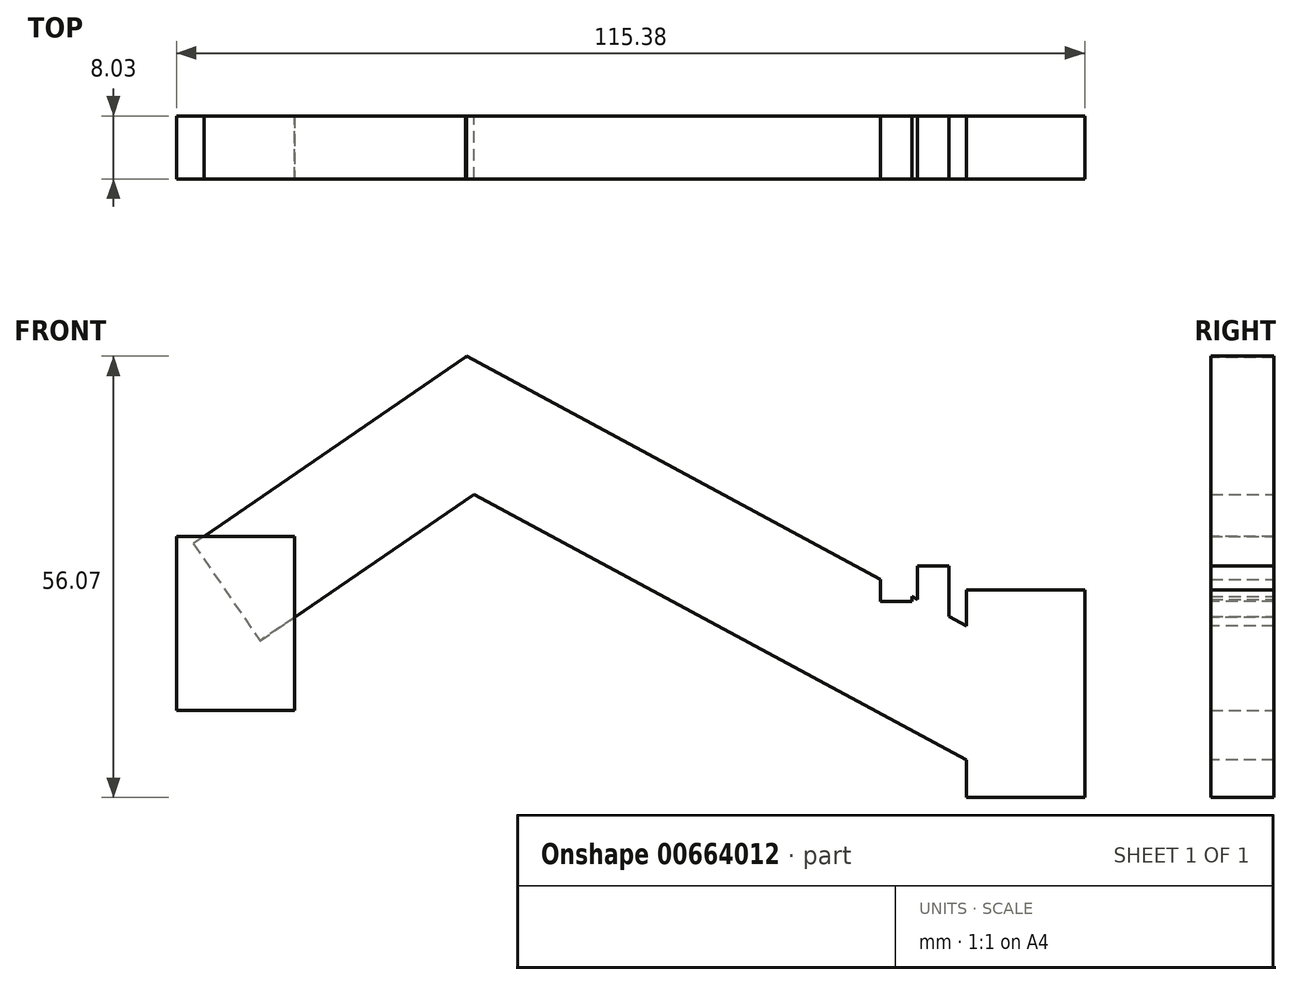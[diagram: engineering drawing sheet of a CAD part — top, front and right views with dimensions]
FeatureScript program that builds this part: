
annotation { "Feature Type Name" : "Feature", "Feature Type Description" : "" }
export const myFeature = defineFeature(function(context is Context, id is Id, definition is map)
    precondition{}
    {
        {
            var Q0;
            Q0=qCreatedBy(makeId("Front.planeOp"),FACE);
            var sketch = newSketch(context, id + "F0", { "sketchPlane" : qUnion([Q0])});
            skLineSegment(sketch, "E0", {"start": v(11.47, -17.68) * mm, "end": v(-10.35, 14.14) * mm});
            skSolve(sketch);
        }
        {
            var Q0;
            Q0=sQuery(id+"F0.wireOp",EDGE,"E0");
            cPlane(context, id + "F1", {"entities" : qUnion([Q0]), "cplaneType" : CPlaneType.LINE_ANGLE, "offset" : 25 * mm, "angle" : 0 * degree, "oppositeDirection" : true, "width" : 150 * mm, "height" : 150 * mm});
        }
        {
            var Q0;
            Q0=qCreatedBy(makeId("Front.planeOp"),FACE);
            var sketch = newSketch(context, id + "F2", { "sketchPlane" : qUnion([Q0])});
            skLineSegment(sketch, "E1", {"start": v(37.84, 33.87) * mm, "end": v(23.91, 8.06) * mm});
            skSolve(sketch);
        }
        {
            var Q0;
            Q0=sQuery(id+"F2.wireOp",EDGE,"E1");
            cPlane(context, id + "F3", {"entities" : qUnion([Q0]), "cplaneType" : CPlaneType.LINE_ANGLE, "offset" : 25 * mm, "angle" : 0 * degree, "width" : 150 * mm, "height" : 150 * mm});
        }
        {
            var Q0;
            Q0=qCreatedBy(id+"F1.planeOp",FACE);
            var sketch = newSketch(context, id + "F4", { "sketchPlane" : qUnion([Q0])});
            skLineSegment(sketch, "E2.bottom", {"start": v(4, 7.5) * mm, "end": v(-4, 7.5) * mm});
            skLineSegment(sketch, "E2.top", {"start": v(4, -7.5) * mm, "end": v(-4, -7.5) * mm});
            skLineSegment(sketch, "E2.left", {"start": v(4, 7.5) * mm, "end": v(4, -7.5) * mm});
            skLineSegment(sketch, "E2.right", {"start": v(-4, 7.5) * mm, "end": v(-4, -7.5) * mm});
            skPoint(sketch, "E2.middle", {"position": v(0, 0) * mm});
            skSolve(sketch);
        }
        {
            var Q0;
            Q0 = qSketchRegion(id + "F4", true);
            extrude(context, id + "F5", {"entities" : qUnion([Q0]), "depth" : 41.9 * mm, "offsetDistance" : 25 * mm});
        }
        {
            var Q0;
            Q0=qCreatedBy(id+"F3.planeOp",FACE);
            var sketch = newSketch(context, id + "F6", { "sketchPlane" : qUnion([Q0])});
            skLineSegment(sketch, "E3.bottom", {"start": v(-4, 40.36) * mm, "end": v(4, 40.36) * mm});
            skLineSegment(sketch, "E3.top", {"start": v(-4, 25.36) * mm, "end": v(4, 25.36) * mm});
            skLineSegment(sketch, "E3.left", {"start": v(-4, 40.36) * mm, "end": v(-4, 25.36) * mm});
            skLineSegment(sketch, "E3.right", {"start": v(4, 40.36) * mm, "end": v(4, 25.36) * mm});
            skPoint(sketch, "E3.middle", {"position": v(0, 32.86) * mm});
            skSolve(sketch);
        }
        {
            var Q0;
            Q0 = qSketchRegion(id + "F6", true);
            extrude(context, id + "F7", {"entities" : qUnion([Q0]), "operationType" : NewBodyOperationType.ADD, "oppositeDirection" : true, "depth" : 84.2 * mm, "offsetDistance" : 25 * mm});
        }
        {
            var Q0;
            Q0 = qSketchRegion(id + "F6", true);
            extrude(context, id + "F8", {"entities" : qUnion([Q0]), "operationType" : NewBodyOperationType.ADD, "depth" : 4.9 * mm, "offsetDistance" : 25 * mm});
        }
        {
            var Q0;
            Q0=qCreatedBy(makeId("Top.planeOp"),FACE);
            var sketch = newSketch(context, id + "F9", { "sketchPlane" : qUnion([Q0])});
            skLineSegment(sketch, "E4.bottom", {"start": v(8.16, -4.03) * mm, "end": v(-6.84, -4.03) * mm});
            skLineSegment(sketch, "E4.top", {"start": v(8.16, 3.97) * mm, "end": v(-6.84, 3.97) * mm});
            skLineSegment(sketch, "E4.left", {"start": v(8.16, -4.03) * mm, "end": v(8.16, 3.97) * mm});
            skLineSegment(sketch, "E4.right", {"start": v(-6.84, -4.03) * mm, "end": v(-6.84, 3.97) * mm});
            skPoint(sketch, "E4.middle", {"position": v(0.66, -0.03) * mm});
            skSolve(sketch);
        }
        {
            var Q0;
            Q0 = qSketchRegion(id + "F9", true);
            extrude(context, id + "F10", {"entities" : qUnion([Q0]), "operationType" : NewBodyOperationType.ADD, "oppositeDirection" : true, "depth" : 15.3 * mm, "offsetDistance" : 25 * mm});
        }
        {
            var Q0;
            Q0 = qSketchRegion(id + "F9", true);
            extrude(context, id + "F11", {"entities" : qUnion([Q0]), "operationType" : NewBodyOperationType.ADD, "depth" : 6.8 * mm, "offsetDistance" : 25 * mm});
        }
        {
            var Q0;
            Q0=qCreatedBy(makeId("Top.planeOp"),FACE);
            var sketch = newSketch(context, id + "F12", { "sketchPlane" : qUnion([Q0])});
            skLineSegment(sketch, "E5.bottom", {"start": v(108.54, -4) * mm, "end": v(93.54, -4) * mm});
            skLineSegment(sketch, "E5.top", {"start": v(108.54, 4) * mm, "end": v(93.54, 4) * mm});
            skLineSegment(sketch, "E5.left", {"start": v(108.54, -4) * mm, "end": v(108.54, 4) * mm});
            skLineSegment(sketch, "E5.right", {"start": v(93.54, -4) * mm, "end": v(93.54, 4) * mm});
            skPoint(sketch, "E5.middle", {"position": v(101.04, 0) * mm});
            skSolve(sketch);
        }
        {
            var Q0;
            Q0 = qSketchRegion(id + "F12", true);
            extrude(context, id + "F13", {"entities" : qUnion([Q0]), "operationType" : NewBodyOperationType.ADD, "oppositeDirection" : true, "depth" : 26.4 * mm, "offsetDistance" : 25 * mm});
        }
        {
            var Q0;
            Q0=qCreatedBy(makeId("Top.planeOp"),FACE);
            var sketch = newSketch(context, id + "F14", { "sketchPlane" : qUnion([Q0])});
            skLineSegment(sketch, "E6.bottom", {"start": v(86.57, 4) * mm, "end": v(82.57, 4) * mm});
            skLineSegment(sketch, "E6.top", {"start": v(86.57, -4) * mm, "end": v(82.57, -4) * mm});
            skLineSegment(sketch, "E6.left", {"start": v(86.57, 4) * mm, "end": v(86.57, -4) * mm});
            skLineSegment(sketch, "E6.right", {"start": v(82.57, 4) * mm, "end": v(82.57, -4) * mm});
            skPoint(sketch, "E6.middle", {"position": v(84.57, 0) * mm});
            skSolve(sketch);
        }
        {
            var Q0;
            Q0=makeQuery(id+"F14.imprint","IMPRINT",FACE,{"disambiguationData":[TD([[makeQuery(id+"F14.imprint","IMPRINT",EDGE,{"derivedFrom":sQuery(id+"F14.wireOp",EDGE,"E6.bottom")}),1.0]])]});
            extrude(context, id + "F15", {"entities" : qUnion([Q0]), "operationType" : NewBodyOperationType.REMOVE, "endBound" : BoundingType.SYMMETRIC, "oppositeDirection" : true, "depth" : 3 * mm, "offsetDistance" : 25 * mm});
        }
        {
            var Q0;
            Q0=qCreatedBy(makeId("Top.planeOp"),FACE);
            var sketch = newSketch(context, id + "F16", { "sketchPlane" : qUnion([Q0])});
            skLineSegment(sketch, "E7.bottom", {"start": v(87.3, 4) * mm, "end": v(91.3, 4) * mm});
            skLineSegment(sketch, "E7.top", {"start": v(87.3, -4) * mm, "end": v(91.3, -4) * mm});
            skLineSegment(sketch, "E7.left", {"start": v(87.3, 4) * mm, "end": v(87.3, -4) * mm});
            skLineSegment(sketch, "E7.right", {"start": v(91.3, 4) * mm, "end": v(91.3, -4) * mm});
            skPoint(sketch, "E7.middle", {"position": v(89.3, 0) * mm});
            skSolve(sketch);
        }
        {
            var Q0;
            Q0 = qSketchRegion(id + "F16", true);
            extrude(context, id + "F17", {"entities" : qUnion([Q0]), "operationType" : NewBodyOperationType.ADD, "oppositeDirection" : true, "depth" : 5 * mm, "offsetDistance" : 25 * mm});
        }
        {
            var Q0;
            Q0 = qSketchRegion(id + "F16", true);
            extrude(context, id + "F18", {"entities" : qUnion([Q0]), "operationType" : NewBodyOperationType.ADD, "depth" : 3 * mm, "offsetDistance" : 25 * mm});
        }
    });
